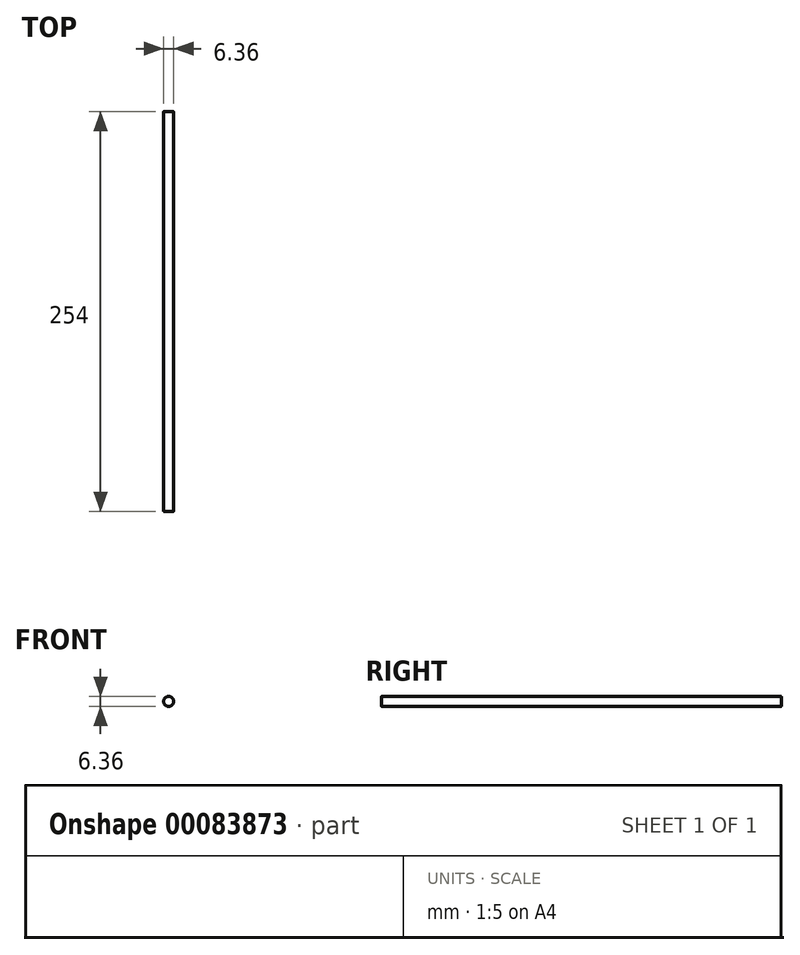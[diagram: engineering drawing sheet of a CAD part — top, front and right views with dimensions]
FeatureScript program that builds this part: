
annotation { "Feature Type Name" : "Feature", "Feature Type Description" : "" }
export const myFeature = defineFeature(function(context is Context, id is Id, definition is map)
    precondition{}
    {
        {
            var Q0;
            Q0=qCreatedBy(makeId("Front.planeOp"),FACE);
            var sketch = newSketch(context, id + "F0", { "sketchPlane" : qUnion([Q0])});
            skCircle(sketch, "E0", {"center": v(0, 0) * mm, "radius": 3.18 * mm});
            skSolve(sketch);
        }
        {
            var Q0;
            Q0=makeQuery(id+"F0.imprint","IMPRINT",FACE,{"disambiguationData":[TD([[makeQuery(id+"F0.imprint","IMPRINT",EDGE,{"derivedFrom":sQuery(id+"F0.wireOp",EDGE,"E0")}),1.0]])]});
            extrude(context, id + "F1", {"entities" : qUnion([Q0]), "depth" : 254 * mm});
        }
        {
            var Q0;
            Q0=makeQuery(id+"F1.opExtrude","CAP_EDGE",EDGE,{"disambiguationData":[OSD([sQuery(id+"F0.wireOp",EDGE,"E0")])],"isStart":false});
            fillet(context, id + "F2", {"entities" : qUnion([Q0]), "radius" : 0.25 * mm, "tangentPropagation" : true, "allowEdgeOverflow" : false});
        }
        {
            var Q0;
            Q0=makeQuery(id+"F1.opExtrude","CAP_EDGE",EDGE,{"disambiguationData":[OSD([sQuery(id+"F0.wireOp",EDGE,"E0")])],"isStart":true});
            fillet(context, id + "F3", {"entities" : qUnion([Q0]), "radius" : 0.25 * mm, "tangentPropagation" : true, "allowEdgeOverflow" : false});
        }
    });
